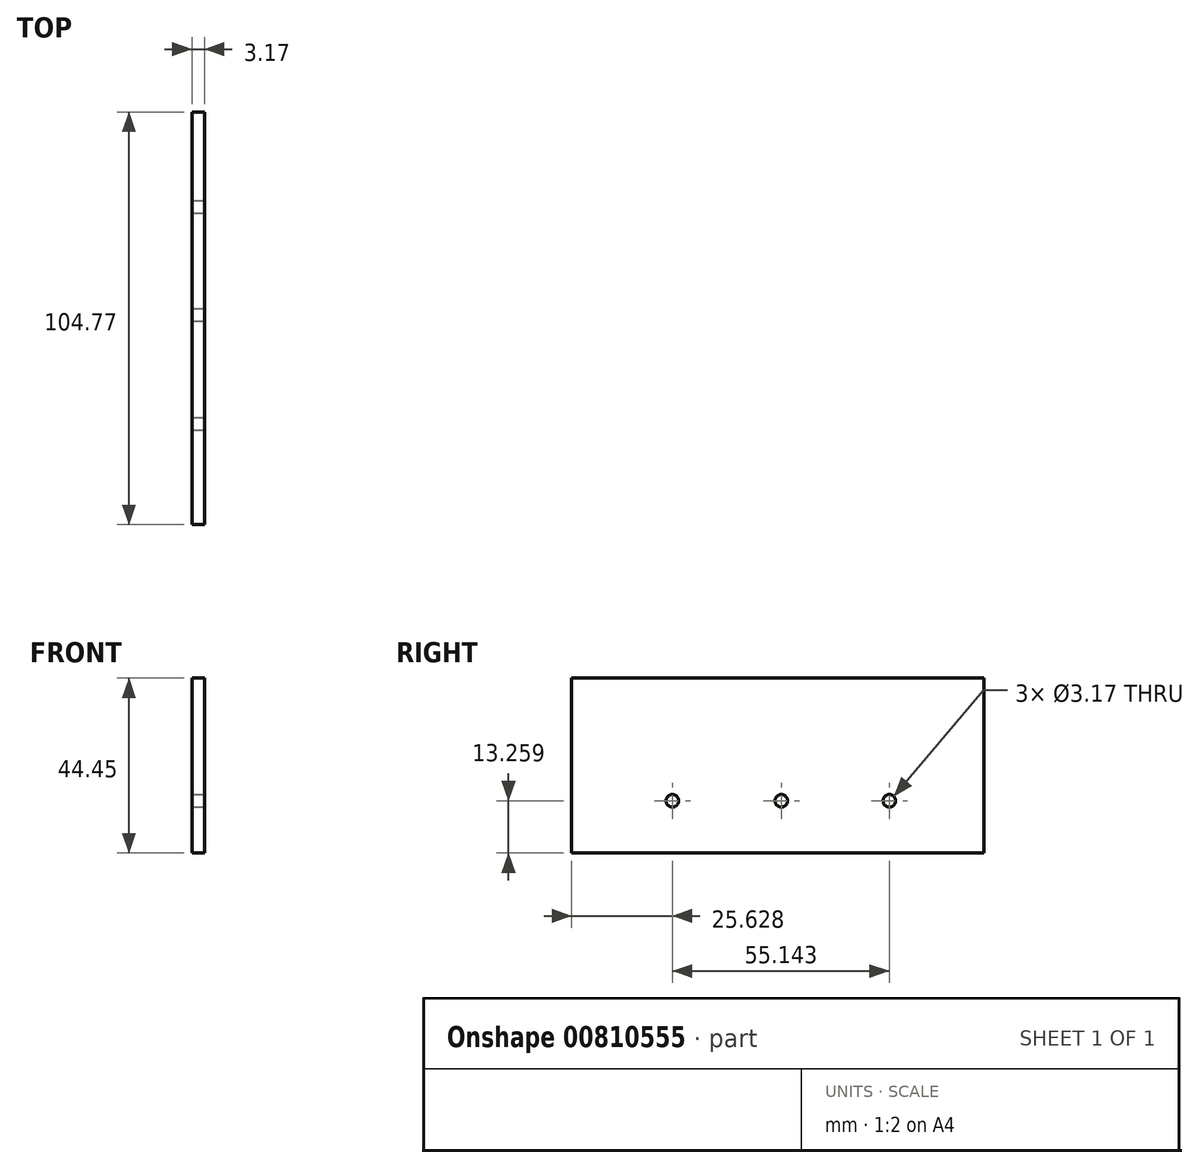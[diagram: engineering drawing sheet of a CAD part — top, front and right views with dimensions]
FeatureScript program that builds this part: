
annotation { "Feature Type Name" : "Feature", "Feature Type Description" : "" }
export const myFeature = defineFeature(function(context is Context, id is Id, definition is map)
    precondition{}
    {
        {
            var Q0;
            Q0=qCreatedBy(makeId("Top.planeOp"),FACE);
            var sketch = newSketch(context, id + "F0", { "sketchPlane" : qUnion([Q0])});
            skLineSegment(sketch, "E0.bottom", {"start": v(20.6, 70.78) * mm, "end": v(23.78, 70.78) * mm});
            skLineSegment(sketch, "E0.top", {"start": v(20.6, -34) * mm, "end": v(23.78, -34) * mm});
            skLineSegment(sketch, "E0.left", {"start": v(20.6, 70.78) * mm, "end": v(20.6, -34) * mm});
            skLineSegment(sketch, "E0.right", {"start": v(23.78, 70.78) * mm, "end": v(23.78, -34) * mm});
            skSolve(sketch);
        }
        {
            var Q0;
            Q0 = qSketchRegion(id + "F0", true);
            extrude(context, id + "F1", {"entities" : qUnion([Q0]), "depth" : 44.45 * mm, "offsetDistance" : 25.4 * mm});
        }
        {
            var Q0;
            Q0=makeQuery(id+"F1.opExtrude","SWEPT_FACE",FACE,{"disambiguationData":[OSD([sQuery(id+"F0.wireOp",EDGE,"E0.right")])]});
            var sketch = newSketch(context, id + "F2", { "sketchPlane" : qUnion([Q0])});
            skLineSegment(sketch, "E1", {"start": v(-9.95, 13.26) * mm, "end": v(-8.36, 13.26) * mm});
            skCircle(sketch, "E2", {"center": v(-8.36, 13.26) * mm, "radius": 1.59 * mm});
            skLineSegment(sketch, "E3", {"start": v(-8.36, 13.26) * mm, "end": v(-6.77, 13.26) * mm});
            skCircle(sketch, "E4", {"center": v(19.32, 13.26) * mm, "radius": 1.59 * mm});
            skLineSegment(sketch, "E5", {"start": v(19.32, 13.26) * mm, "end": v(20.91, 13.26) * mm});
            skCircle(sketch, "E6", {"center": v(46.78, 13.26) * mm, "radius": 1.59 * mm});
            skLineSegment(sketch, "E7.trimOffspring", {"start": v(17.74, 13.26) * mm, "end": v(19.32, 13.26) * mm});
            skLineSegment(sketch, "E8.trimOffspring", {"start": v(45.2, 13.26) * mm, "end": v(46.78, 13.26) * mm});
            skSolve(sketch);
        }
        {
            var Q0;
            Q0 = qSketchRegion(id + "F2", true);
            extrude(context, id + "F3", {"entities" : qUnion([Q0]), "operationType" : NewBodyOperationType.REMOVE, "oppositeDirection" : true, "depth" : 152.4 * mm, "offsetDistance" : 25.4 * mm});
        }
    });
